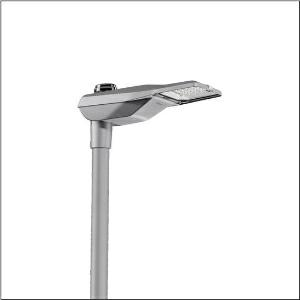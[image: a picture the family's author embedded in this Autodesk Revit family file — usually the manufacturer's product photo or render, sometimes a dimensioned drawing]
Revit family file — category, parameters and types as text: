
# Revit family: streetlight_sl_21_micro___st0_8a_5xe5c47n08db_8458
name_source: partatom
category: Lighting Fixtures
units: mm (PartAtom-declared; Revit-internal decimal feet)

## family parameters
Cut with Voids When Loaded = No
Host = Face
Light Source = No
Part Type = Normal
Room Calculation Point = No
Round Connector Dimension = Use Diameter
Shared = No

## types (1)
- --- (1 x LED, 5320 lm, 39.1 W, 4000K)
    Apparent Load = 39 VA
    CIE Flux Codes = 38 75 97 100 100
    Color Rendering = 70
    Color Temperature = 4000K
    Default Elevation = 1800 mm
    Description = Streetlight SL 21 micro, mast luminaire, primary light control with lens, of PMMA, primary optical cover: cover, of toughened safety glass, transparent, light distribution: ST0.8a, light emission: direct distribution, primary light characteristic: asymmetric, installation type: post-top, LED, 3G 1.5mm², High Power LED, rated luminous flux: 5.320lm, luminous efficacy: 136lm/W, light colour: 740, colour temperature: 4000K, control: overheat protection, pre-setting: linear dimming characteristic, constant luminous flux control, time-dependent luminous flux control, flexible luminous flux parameterisation, mains connection: 230..240V, AC, 50/60Hz, connection cable pre-assembled, cable length: 6,5m, wiring characteristics: H07RN-F, start of lifetime: 39W, end of service life: 41W, reduction: 18W, luminaire housing, of diecast aluminium (EN AC-44300), powder-coated, Siteco® metallic grey (DB 702S), corrosivity category C5 mid according to DIN EN ISO 12944, multi-level sealing system, sealing non-destructively replaceable, inclination adjustable: 0°, 5°, 10°, 15°, length: 528mm, width: 235mm, height: 110mm, spigot size: 76/60mm (post-top), protection rating (complete): IP66, insulation class (complete): insulation class I (protective earthing), certification: CE, ENEC, ENEC+, VDE, impact resistance: IK09, permissible operating ambient temperature for outdoor applications: -40..+50°C, standard-compliant lighting for roads and squares, packaging unit: 1 piece

Light Distribution: ST0.8a
    Height = 110 mm
    Lamp = 1 x LED
    Lamp Light Flux = 5320 lm
    Lamp Power = 39.1 W
    Lamp count = 1
    Length = 528 mm
    Luminous efficacy = 136 lm/W
    Manufacturer = Siteco
    ModVariant = No
    Model = 5XE5C47N08DB
    Number of Poles = 1
    OnlyDefault = Yes
    Power Factor = 1
    Product Name = Streetlight SL 21 micro | ST0.8a
    Product group = mast luminaire | pylon top
    ProductGroupID = 6100
    Protection Class = Protection class I
    Protection Degree = IP 66
    RLX_Detail_Level = 1
    RLX_Emergency_Light_Flux = 0 lm
    RLX_Emergency_Type = 0
    RLX_Emergency_Type_DB = No
    RlxData = <blob elided: 98897 chars, md5=39305d18>
    Socket = socket
    Standby Power = 0 W
    System Light Flux = 5320 lm
    System Power = 39 W
    Type Comments = factory setting: luminous flux: 100 % | dim-lin: 254 | 765 mA
    Type Image = l_1294375.jpg
    URL = http://relux.com
    VarID = @adj_104107
    Voltage = 0 V
    Weight = 0.00 kg
    Width = 235 mm

## geometry (parser evidence)
native form markers: Blend x4, Sweep x9
no freeform markers — native parametric forms only
